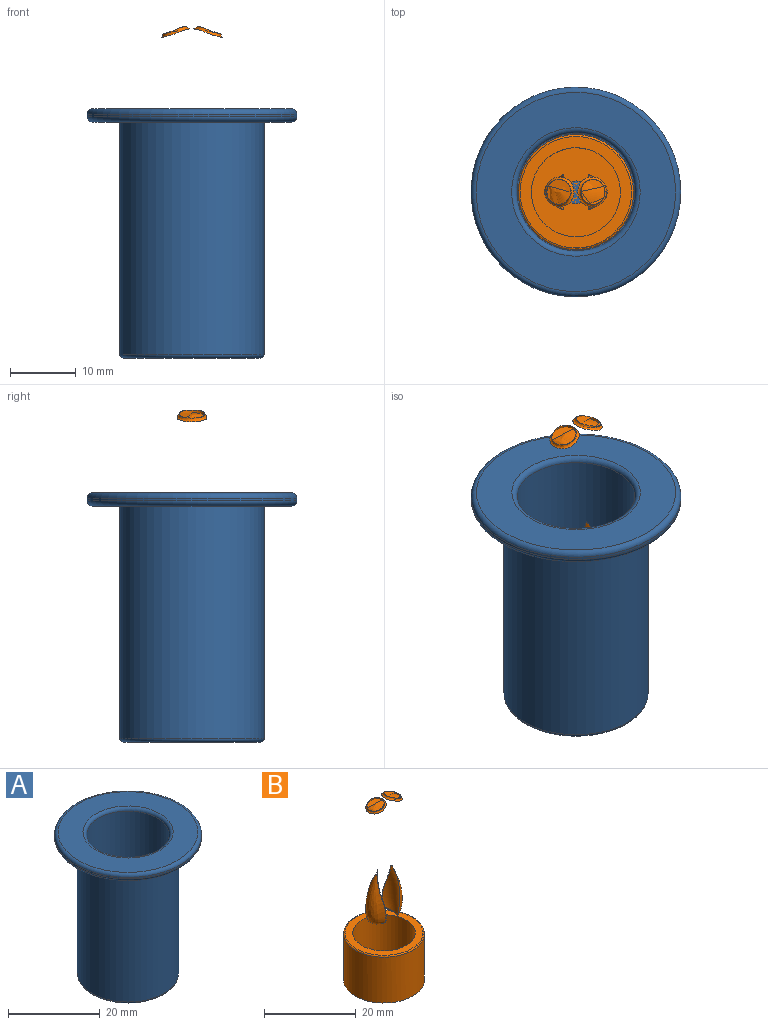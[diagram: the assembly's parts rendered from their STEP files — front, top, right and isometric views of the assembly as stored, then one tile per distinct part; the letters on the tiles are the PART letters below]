
ASSEMBLY  parts=2 mates=1
PART A: 11 faces, bbox 34.6x34.6x38 mm
  f0: cylinder r=9mm len=35.2mm, axis (0,0,1), area 1990.5mm2, adj f1,f9
  f1: plane 18x18mm, normal (0,0,1), area 254.5mm2, adj f0
  f2: plane 21x21mm, normal (0,0,-1), area 346.4mm2, adj f10
  f3: cylinder r=11mm len=35.5mm, axis (0,0,1), area 2453.6mm2, adj f4,f10
  f4: plane 30.4x30.4mm, normal (0,0,-1), area 345.7mm2, adj f3,f5
  f5: torus R=15.2mm, axis (0,0,1), area 124mm2, adj f4,f6
  f6: cylinder r=16mm len=32mm, axis (0,0,1), area 40.2mm2, adj f5,f7
  f7: torus R=15.2mm, axis (0,0,1), area 124mm2, adj f6,f8
  f8: plane 30.4x30.4mm, normal (0,0,1), area 424.1mm2, adj f7,f9
  f9: torus R=9.8mm, axis (0,0,1), area 73.4mm2, adj f0,f8
  f10: torus R=10.5mm, axis (0,0,1), area 53.4mm2, adj f2,f3
PART B: 16 faces, bbox 19.2x19.2x48.7 mm
  f0: revolved ~46.21x19.24mm, area 1326.8mm2, adj f1,f3,f9,f11
  f1: bspline ~12.64x5.3mm, area 3mm2, adj f0,f2
  f2: bspline ~15.64x11.96mm, area 69.6mm2, adj f1
  f3: plane 13.6x13.6mm, normal (0,0,1), area 135.7mm2, adj f0,f4
  f4: cylinder r=6.8mm len=13.6mm, axis (0,0,-1), area 448.6mm2, adj f3,f5
  f5: plane 17x17mm, normal (0,0,1), area 81.7mm2, adj f4,f6
  f6: torus R=8.5mm, axis (0,0,1), area 25.7mm2, adj f5,f7
  f7: cylinder r=8.8mm len=17.6mm, axis (0,0,-1), area 674.6mm2, adj f6,f8
  f8: plane 17.6x17.6mm, normal (0,0,-1), area 243.3mm2, adj f7
  f9: bspline ~12.64x5.3mm, area 3mm2, adj f0,f10
  f10: bspline ~12.48x5.27mm, area 69.7mm2, adj f9
  f11: bspline ~4.52x4.37mm, area 8.9mm2, adj f0,f12
  f12: revolved ~3.87x3.84mm, area 2.7mm2, adj f11
  f13: revolved ~8.34x4.53mm, area 16.8mm2, adj f14
  f14: bspline ~4.52x4.37mm, area 8.9mm2, adj f13,f15
  f15: revolved ~3.87x3.84mm, area 2.7mm2, adj f14
PLACE A t=(-4.61,4.2,-6.7)mm fixed
PLACE B t=(-4.61,4.2,-6.7)mm
MATE slider B.f4 <-> A.f0  axis (0,0,-1) through (-4.61,4.2,-6.7)mm
